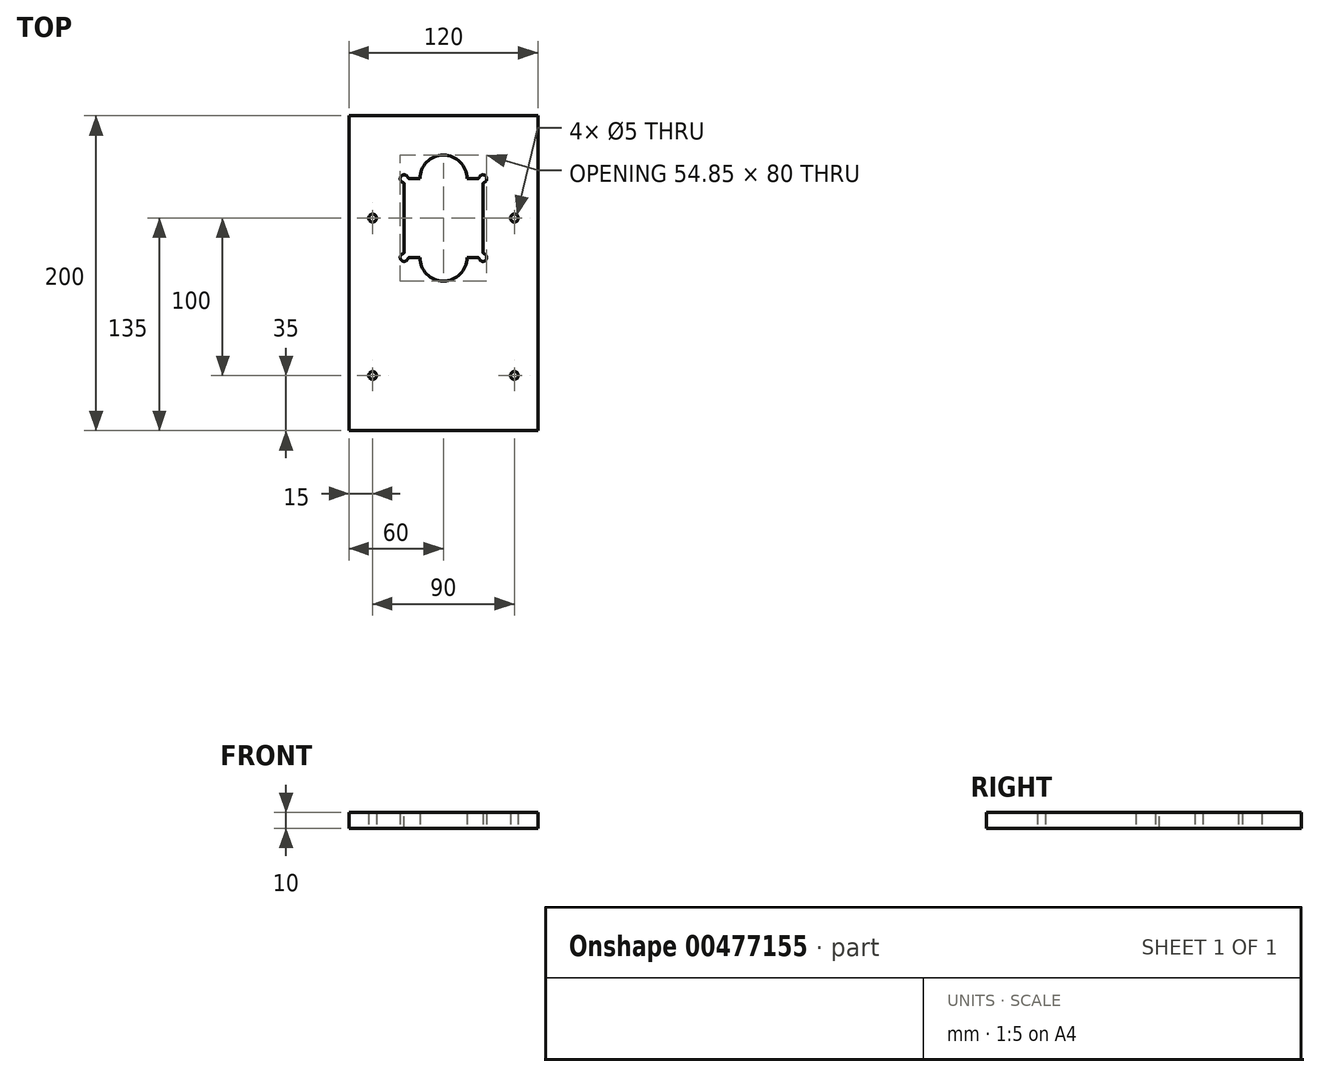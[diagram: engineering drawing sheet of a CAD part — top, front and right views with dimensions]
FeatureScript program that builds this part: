
annotation { "Feature Type Name" : "Feature", "Feature Type Description" : "" }
export const myFeature = defineFeature(function(context is Context, id is Id, definition is map)
    precondition{}
    {
        {
            var Q0;
            Q0=qCreatedBy(makeId("Top.planeOp"),FACE);
            var sketch = newSketch(context, id + "F0", { "sketchPlane" : qUnion([Q0])});
            skLineSegment(sketch, "E0.bottom", {"start": v(-60, 65) * mm, "end": v(60, 65) * mm});
            skLineSegment(sketch, "E0.top", {"start": v(-60, -135) * mm, "end": v(60, -135) * mm});
            skLineSegment(sketch, "E0.left", {"start": v(-60, 65) * mm, "end": v(-60, -135) * mm});
            skLineSegment(sketch, "E0.right", {"start": v(60, 65) * mm, "end": v(60, -135) * mm});
            skLineSegment(sketch, "E1.bottom", {"start": v(25, -25) * mm, "end": v(-25, -25) * mm});
            skLineSegment(sketch, "E1.top", {"start": v(25, 25) * mm, "end": v(-25, 25) * mm});
            skLineSegment(sketch, "E1.left", {"start": v(25, -25) * mm, "end": v(25, 25) * mm});
            skLineSegment(sketch, "E1.right", {"start": v(-25, -25) * mm, "end": v(-25, 25) * mm});
            skCircle(sketch, "E2", {"center": v(45, -100) * mm, "radius": 2.5 * mm});
            skCircle(sketch, "E3", {"center": v(-45, -100) * mm, "radius": 2.5 * mm});
            skCircle(sketch, "E4", {"center": v(-25, 25) * mm, "radius": 2.5 * mm});
            skCircle(sketch, "E5", {"center": v(25, 25) * mm, "radius": 2.5 * mm});
            skCircle(sketch, "E6", {"center": v(-25, -25) * mm, "radius": 2.5 * mm});
            skCircle(sketch, "E7", {"center": v(25, -25) * mm, "radius": 2.5 * mm});
            skCircle(sketch, "E8", {"center": v(0, 25) * mm, "radius": 15 * mm});
            skCircle(sketch, "E9", {"center": v(0, -25) * mm, "radius": 15 * mm});
            skPoint(sketch, "E10", {"position": v(-45, 0) * mm});
            skPoint(sketch, "E10.positionSnap0", {"position": v(-25, 0) * mm});
            skPoint(sketch, "E11", {"position": v(45, 0) * mm});
            skCircle(sketch, "E12", {"center": v(-45, 0) * mm, "radius": 2.5 * mm});
            skCircle(sketch, "E13", {"center": v(45, 0) * mm, "radius": 2.5 * mm});
            skSolve(sketch);
        }
        {
            var Q0;
            Q0=qSketchRegion(id+"F0",true);
            extrude(context, id + "F1", {"entities" : qUnion([Q0]), "depth" : 10 * mm});
        }
        {
            var Q0;
            Q0=makeQuery(id+"F1.opExtrude","SWEPT_EDGE",EDGE,{"disambiguationData":[OSD([sQuery(id+"F0.wireOp",EDGE,"E1.top"),sQuery(id+"F0.wireOp",EDGE,"E4")])]});
            var Q1;
            Q1=makeQuery(id+"F1.opExtrude","SWEPT_EDGE",EDGE,{"disambiguationData":[OSD([sQuery(id+"F0.wireOp",EDGE,"E1.right"),sQuery(id+"F0.wireOp",EDGE,"E4")])]});
            var Q2;
            Q2=makeQuery(id+"F1.opExtrude","SWEPT_EDGE",EDGE,{"disambiguationData":[OSD([sQuery(id+"F0.wireOp",EDGE,"E1.right"),sQuery(id+"F0.wireOp",EDGE,"E6")])]});
            var Q3;
            Q3=makeQuery(id+"F1.opExtrude","SWEPT_EDGE",EDGE,{"disambiguationData":[OSD([sQuery(id+"F0.wireOp",EDGE,"E1.bottom"),sQuery(id+"F0.wireOp",EDGE,"E6")])]});
            var Q4;
            Q4=makeQuery(id+"F1.opExtrude","SWEPT_EDGE",EDGE,{"disambiguationData":[OSD([sQuery(id+"F0.wireOp",EDGE,"E1.top"),sQuery(id+"F0.wireOp",EDGE,"E5")])]});
            var Q5;
            Q5=makeQuery(id+"F1.opExtrude","SWEPT_EDGE",EDGE,{"disambiguationData":[OSD([sQuery(id+"F0.wireOp",EDGE,"E1.left"),sQuery(id+"F0.wireOp",EDGE,"E5")])]});
            var Q6;
            Q6=makeQuery(id+"F1.opExtrude","SWEPT_EDGE",EDGE,{"disambiguationData":[OSD([sQuery(id+"F0.wireOp",EDGE,"E1.bottom"),sQuery(id+"F0.wireOp",EDGE,"E7")])]});
            var Q7;
            Q7=makeQuery(id+"F1.opExtrude","SWEPT_EDGE",EDGE,{"disambiguationData":[OSD([sQuery(id+"F0.wireOp",EDGE,"E1.left"),sQuery(id+"F0.wireOp",EDGE,"E7")])]});
            fillet(context, id + "F2", {"entities" : qUnion([Q0, Q1, Q2, Q3, Q4, Q5, Q6, Q7]), "radius" : 1 * mm, "tangentPropagation" : true, "allowEdgeOverflow" : false});
        }
    });
